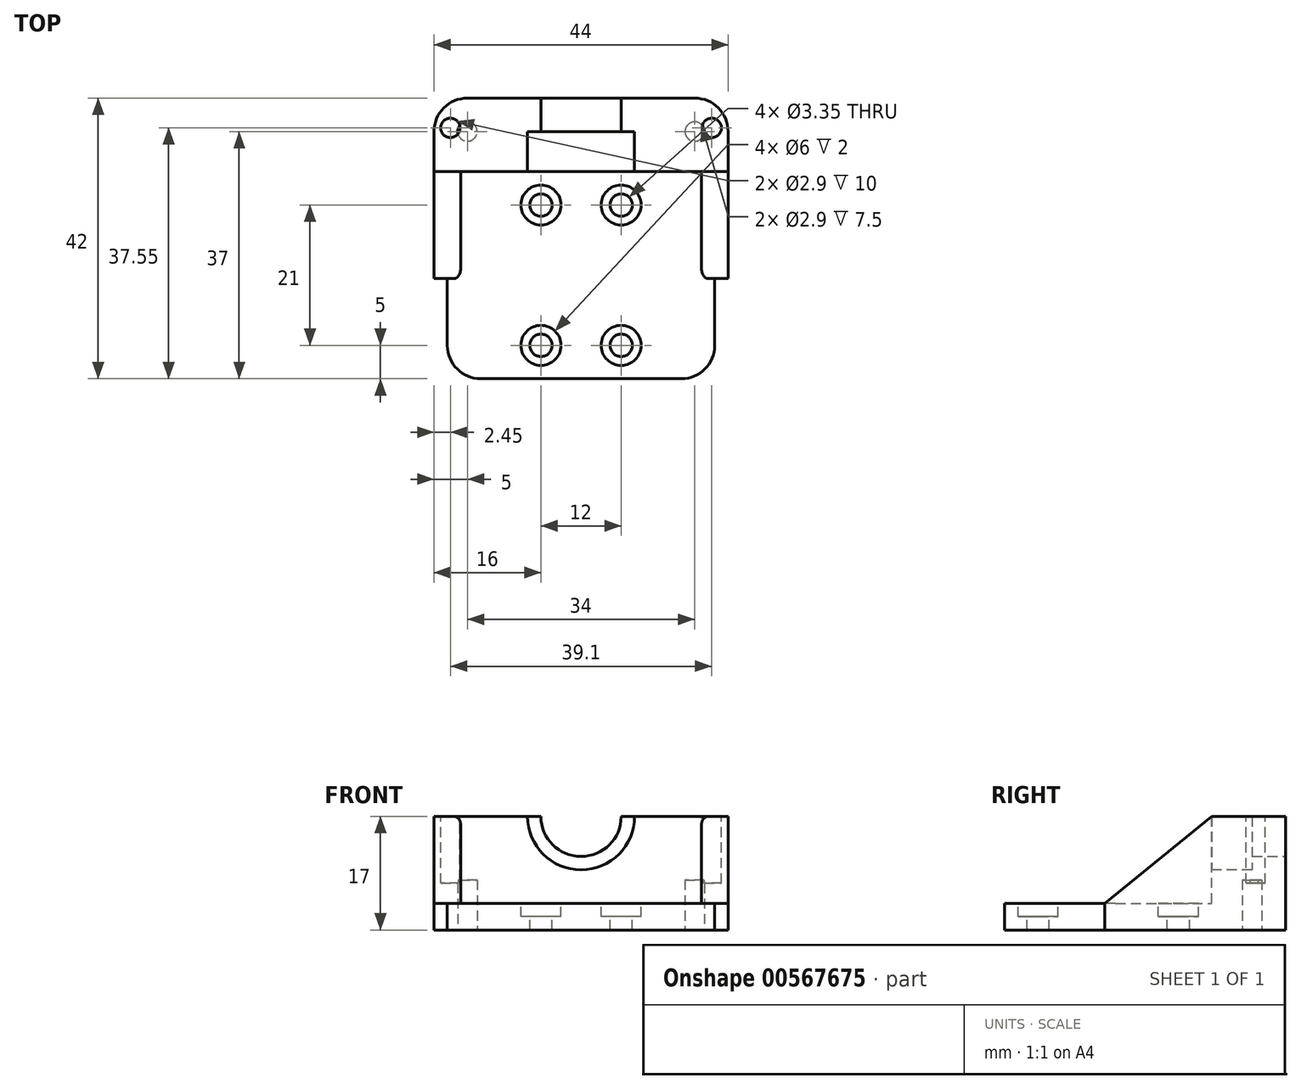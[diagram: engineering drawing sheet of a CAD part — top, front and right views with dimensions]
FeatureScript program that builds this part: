
annotation { "Feature Type Name" : "Feature", "Feature Type Description" : "" }
export const myFeature = defineFeature(function(context is Context, id is Id, definition is map)
    precondition{}
    {
        {
            var Q0;
            Q0=qCreatedBy(makeId("Top.planeOp"),FACE);
            var sketch = newSketch(context, id + "F0", { "sketchPlane" : qUnion([Q0])});
            skLineSegment(sketch, "E0.bottom", {"start": v(0, 0) * mm, "end": v(40, 0) * mm});
            skLineSegment(sketch, "E0.top", {"start": v(0, 42) * mm, "end": v(40, 42) * mm});
            skLineSegment(sketch, "E0.left", {"start": v(0, 0) * mm, "end": v(0, 42) * mm});
            skLineSegment(sketch, "E0.right", {"start": v(40, 0) * mm, "end": v(40, 42) * mm});
            skSolve(sketch);
        }
        {
            var Q0;
            Q0=qSketchRegion(id+"F0",true);
            extrude(context, id + "F1", {"entities" : qUnion([Q0]), "depth" : 4 * mm});
        }
        {
            var Q0;
            Q0=makeQuery(id+"F1.opExtrude","CAP_FACE",FACE,{"disambiguationData":[OSD([sQuery(id+"F0.wireOp",EDGE,"E0.bottom"),sQuery(id+"F0.wireOp",EDGE,"E0.top"),sQuery(id+"F0.wireOp",EDGE,"E0.left"),sQuery(id+"F0.wireOp",EDGE,"E0.right")])],"isStart":false});
            var sketch = newSketch(context, id + "F2", { "sketchPlane" : qUnion([Q0])});
            skCircle(sketch, "E1", {"center": v(14, 26) * mm, "radius": 1.68 * mm});
            skCircle(sketch, "E2", {"center": v(26, 26) * mm, "radius": 1.68 * mm});
            skCircle(sketch, "E3", {"center": v(14, 5) * mm, "radius": 1.68 * mm});
            skCircle(sketch, "E4", {"center": v(26, 5) * mm, "radius": 1.68 * mm});
            skLineSegment(sketch, "E5", {"start": v(14, 26) * mm, "end": v(0, 26) * mm});
            skLineSegment(sketch, "E6", {"start": v(26, 5) * mm, "end": v(40, 5) * mm});
            skCircle(sketch, "E7", {"center": v(14, 26) * mm, "radius": 3 * mm});
            skCircle(sketch, "E8", {"center": v(26, 26) * mm, "radius": 3 * mm});
            skCircle(sketch, "E9", {"center": v(14, 5) * mm, "radius": 3 * mm});
            skCircle(sketch, "E10", {"center": v(26, 5) * mm, "radius": 3 * mm});
            skSolve(sketch);
        }
        {
            var Q0;
            Q0=makeQuery(id+"F2.imprint","IMPRINT",FACE,{"disambiguationData":[TD([[makeQuery(id+"F2.imprint","IMPRINT",EDGE,{"derivedFrom":sQuery(id+"F2.wireOp",EDGE,"E1")}),1.0]])]});
            var Q1;
            Q1=makeQuery(id+"F2.imprint","IMPRINT",FACE,{"disambiguationData":[TD([[makeQuery(id+"F2.imprint","IMPRINT",EDGE,{"derivedFrom":sQuery(id+"F2.wireOp",EDGE,"E2")}),1.0]])]});
            var Q2;
            Q2=makeQuery(id+"F2.imprint","IMPRINT",FACE,{"disambiguationData":[TD([[makeQuery(id+"F2.imprint","IMPRINT",EDGE,{"derivedFrom":sQuery(id+"F2.wireOp",EDGE,"E4")}),1.0]])]});
            var Q3;
            Q3=makeQuery(id+"F2.imprint","IMPRINT",FACE,{"disambiguationData":[TD([[makeQuery(id+"F2.imprint","IMPRINT",EDGE,{"derivedFrom":sQuery(id+"F2.wireOp",EDGE,"E3")}),1.0]])]});
            extrude(context, id + "F3", {"entities" : qUnion([Q0, Q1, Q2, Q3]), "operationType" : NewBodyOperationType.REMOVE, "oppositeDirection" : true, "depth" : 25 * mm});
        }
        {
            var Q0;
            Q0=makeQuery(id+"F1.opExtrude","CAP_FACE",FACE,{"disambiguationData":[OSD([sQuery(id+"F0.wireOp",EDGE,"E0.bottom"),sQuery(id+"F0.wireOp",EDGE,"E0.top"),sQuery(id+"F0.wireOp",EDGE,"E0.left"),sQuery(id+"F0.wireOp",EDGE,"E0.right")])],"isStart":false});
            var sketch = newSketch(context, id + "F4", { "sketchPlane" : qUnion([Q0])});
            skLineSegment(sketch, "E11.bottom", {"start": v(0, 42) * mm, "end": v(40, 42) * mm});
            skLineSegment(sketch, "E11.top", {"start": v(0, 31) * mm, "end": v(40, 31) * mm});
            skLineSegment(sketch, "E11.left", {"start": v(0, 42) * mm, "end": v(0, 31) * mm});
            skLineSegment(sketch, "E11.right", {"start": v(40, 42) * mm, "end": v(40, 31) * mm});
            skSolve(sketch);
        }
        {
            var Q0;
            Q0=qSketchRegion(id+"F4",true);
            extrude(context, id + "F5", {"entities" : qUnion([Q0]), "operationType" : NewBodyOperationType.ADD, "depth" : 13 * mm, "offsetDistance" : 25 * mm});
        }
        {
            var Q0;
            Q0=makeQuery(id+"F5.boolean.opBoolean","MERGE",FACE,{"derivedFrom":[makeQuery(id+"F1.opExtrude","SWEPT_FACE",FACE,{"disambiguationData":[OSD([sQuery(id+"F0.wireOp",EDGE,"E0.top")])]}),makeQuery(id+"F5.opExtrude","SWEPT_FACE",FACE,{"disambiguationData":[OSD([sQuery(id+"F4.wireOp",EDGE,"E11.bottom")])]})]});
            var sketch = newSketch(context, id + "F6", { "sketchPlane" : qUnion([Q0])});
            skCircle(sketch, "E12", {"center": v(-20, 17) * mm, "radius": 6 * mm});
            skSolve(sketch);
        }
        {
            var Q0;
            {var subQ0=makeQuery(id+"F5.opExtrude","CAP_EDGE",EDGE,{"disambiguationData":[OSD([sQuery(id+"F4.wireOp",EDGE,"E11.bottom")])],"isStart":false});var subQ1=sQuery(id+"F6.wireOp",EDGE,"E12");var subQ3=makeQuery(id+"F6.imprint","INTERSECT",VERTEX,{"disambiguationData":[OD(0.0)],"derivedFrom":[subQ0,subQ1]});Q0=makeQuery(id+"F6.imprint","IMPRINT",FACE,{"disambiguationData":[TD([[makeQuery(id+"F6.imprint","IMPRINT",EDGE,{"disambiguationData":[TD([[subQ3,1.0]])],"derivedFrom":subQ1}),1.0]])]});}
            extrude(context, id + "F7", {"entities" : qUnion([Q0]), "operationType" : NewBodyOperationType.REMOVE, "oppositeDirection" : true, "depth" : 6 * mm});
        }
        {
            var Q0;
            Q0=makeQuery(id+"F5.opExtrude","SWEPT_FACE",FACE,{"disambiguationData":[OSD([sQuery(id+"F4.wireOp",EDGE,"E11.top")])]});
            var sketch = newSketch(context, id + "F8", { "sketchPlane" : qUnion([Q0])});
            skCircle(sketch, "E13", {"center": v(20, 17) * mm, "radius": 8 * mm});
            skSolve(sketch);
        }
        {
            var Q0;
            Q0=qSketchRegion(id+"F8",true);
            extrude(context, id + "F9", {"entities" : qUnion([Q0]), "operationType" : NewBodyOperationType.REMOVE, "oppositeDirection" : true, "depth" : 6 * mm});
        }
        {
            var Q0;
            Q0=makeQuery(id+"F2.imprint","IMPRINT",FACE,{"disambiguationData":[TD([[makeQuery(id+"F2.imprint","IMPRINT",EDGE,{"derivedFrom":sQuery(id+"F2.wireOp",EDGE,"E1")}),-1.0]])]});
            var Q1;
            Q1=makeQuery(id+"F2.imprint","IMPRINT",FACE,{"disambiguationData":[TD([[makeQuery(id+"F2.imprint","IMPRINT",EDGE,{"derivedFrom":sQuery(id+"F2.wireOp",EDGE,"E2")}),-1.0]])]});
            var Q2;
            Q2=makeQuery(id+"F2.imprint","IMPRINT",FACE,{"disambiguationData":[TD([[makeQuery(id+"F2.imprint","IMPRINT",EDGE,{"derivedFrom":sQuery(id+"F2.wireOp",EDGE,"E4")}),-1.0]])]});
            var Q3;
            Q3=makeQuery(id+"F2.imprint","IMPRINT",FACE,{"disambiguationData":[TD([[makeQuery(id+"F2.imprint","IMPRINT",EDGE,{"derivedFrom":sQuery(id+"F2.wireOp",EDGE,"E3")}),-1.0]])]});
            extrude(context, id + "F10", {"entities" : qUnion([Q0, Q1, Q2, Q3]), "operationType" : NewBodyOperationType.REMOVE, "oppositeDirection" : true, "depth" : 2 * mm});
        }
        {
            var Q0;
            Q0=makeQuery(id+"F5.boolean.opBoolean","MERGE",FACE,{"derivedFrom":[makeQuery(id+"F1.opExtrude","SWEPT_FACE",FACE,{"disambiguationData":[OSD([sQuery(id+"F0.wireOp",EDGE,"E0.left")])]}),makeQuery(id+"F5.opExtrude","SWEPT_FACE",FACE,{"disambiguationData":[OSD([sQuery(id+"F4.wireOp",EDGE,"E11.left")])]})]});
            var sketch = newSketch(context, id + "F11", { "sketchPlane" : qUnion([Q0])});
            skLineSegment(sketch, "E14.bottom", {"start": v(-42, 0) * mm, "end": v(-31, 0) * mm});
            skLineSegment(sketch, "E14.top", {"start": v(-42, 17) * mm, "end": v(-31, 17) * mm});
            skLineSegment(sketch, "E14.left", {"start": v(-42, 0) * mm, "end": v(-42, 17) * mm});
            skLineSegment(sketch, "E14.right", {"start": v(-31, 0) * mm, "end": v(-31, 17) * mm});
            skSolve(sketch);
        }
        {
            var Q0;
            Q0=qSketchRegion(id+"F11",true);
            extrude(context, id + "F12", {"entities" : qUnion([Q0]), "operationType" : NewBodyOperationType.ADD, "depth" : 2 * mm});
        }
        {
            var Q0;
            Q0=makeQuery(id+"F1.opExtrude","SWEPT_EDGE",EDGE,{"disambiguationData":[OSD([sQuery(id+"F0.wireOp",EDGE,"E0.bottom"),sQuery(id+"F0.wireOp",EDGE,"E0.left")])]});
            var Q1;
            Q1=makeQuery(id+"F1.opExtrude","SWEPT_EDGE",EDGE,{"disambiguationData":[OSD([sQuery(id+"F0.wireOp",EDGE,"E0.bottom"),sQuery(id+"F0.wireOp",EDGE,"E0.right")])]});
            var Q2;
            Q2=makeQuery(id+"F17.opExtrude","TWEAK_EDGE",EDGE,{"derivedFrom":[makeQuery(id+"F1.opExtrude","SWEPT_EDGE",EDGE,{"disambiguationData":[OSD([sQuery(id+"F0.wireOp",EDGE,"E0.bottom"),sQuery(id+"F0.wireOp",EDGE,"E0.left")])]}),makeQuery(id+"F12.opExtrude","CAP_FACE",FACE,{"disambiguationData":[OSD([sQuery(id+"F11.wireOp",EDGE,"E14.bottom"),sQuery(id+"F11.wireOp",EDGE,"E14.top"),sQuery(id+"F11.wireOp",EDGE,"E14.left"),sQuery(id+"F11.wireOp",EDGE,"E14.right")])],"isStart":false})]});
            fillet(context, id + "F13", {"entities" : qUnion([Q0, Q1, Q2]), "radius" : 5 * mm, "tangentPropagation" : true, "allowEdgeOverflow" : false});
        }
        {
            var Q0;
            Q0=makeQuery(id+"F5.boolean.opBoolean","MERGE",FACE,{"derivedFrom":[makeQuery(id+"F1.opExtrude","SWEPT_FACE",FACE,{"disambiguationData":[OSD([sQuery(id+"F0.wireOp",EDGE,"E0.right")])]}),makeQuery(id+"F5.opExtrude","SWEPT_FACE",FACE,{"disambiguationData":[OSD([sQuery(id+"F4.wireOp",EDGE,"E11.right")])]})]});
            var sketch = newSketch(context, id + "F14", { "sketchPlane" : qUnion([Q0])});
            skLineSegment(sketch, "E15.bottom", {"start": v(42, 0) * mm, "end": v(31, 0) * mm});
            skLineSegment(sketch, "E15.top", {"start": v(42, 17) * mm, "end": v(31, 17) * mm});
            skLineSegment(sketch, "E15.left", {"start": v(42, 0) * mm, "end": v(42, 17) * mm});
            skLineSegment(sketch, "E15.right", {"start": v(31, 0) * mm, "end": v(31, 17) * mm});
            skSolve(sketch);
        }
        {
            var Q0;
            Q0=qSketchRegion(id+"F14",true);
            extrude(context, id + "F15", {"entities" : qUnion([Q0]), "operationType" : NewBodyOperationType.ADD, "depth" : 2 * mm});
        }
        {
            var Q0;
            Q0=qSketchRegion(id+"F14",true);
            extrude(context, id + "F16", {"entities" : qUnion([Q0]), "operationType" : NewBodyOperationType.ADD, "depth" : 2 * mm});
        }
        {
            var Q0;
            Q0=makeQuery(id+"F5.boolean.opBoolean","MERGE",FACE,{"derivedFrom":[makeQuery(id+"F1.opExtrude","SWEPT_FACE",FACE,{"disambiguationData":[OSD([sQuery(id+"F0.wireOp",EDGE,"E0.left")])]}),makeQuery(id+"F5.opExtrude","SWEPT_FACE",FACE,{"disambiguationData":[OSD([sQuery(id+"F4.wireOp",EDGE,"E11.left")])]})]});
            var Q1;
            Q1=makeQuery(id+"F12.opExtrude","CAP_FACE",FACE,{"disambiguationData":[OSD([sQuery(id+"F11.wireOp",EDGE,"E14.bottom"),sQuery(id+"F11.wireOp",EDGE,"E14.top"),sQuery(id+"F11.wireOp",EDGE,"E14.left"),sQuery(id+"F11.wireOp",EDGE,"E14.right")])],"isStart":false});
            extrude(context, id + "F17", {"entities" : qUnion([Q0]), "operationType" : NewBodyOperationType.ADD, "endBound" : BoundingType.UP_TO_SURFACE, "depth" : 25 * mm, "endBoundEntityFace" : qUnion([Q1]), "offsetDistance" : 25 * mm});
        }
        {
            var Q0;
            Q0=makeQuery(id+"F5.boolean.opBoolean","MERGE",FACE,{"derivedFrom":[makeQuery(id+"F1.opExtrude","SWEPT_FACE",FACE,{"disambiguationData":[OSD([sQuery(id+"F0.wireOp",EDGE,"E0.right")])]}),makeQuery(id+"F5.opExtrude","SWEPT_FACE",FACE,{"disambiguationData":[OSD([sQuery(id+"F4.wireOp",EDGE,"E11.right")])]})]});
            var Q1;
            Q1=makeQuery(id+"F15.opExtrude","CAP_FACE",FACE,{"disambiguationData":[OSD([sQuery(id+"F14.wireOp",EDGE,"E15.bottom"),sQuery(id+"F14.wireOp",EDGE,"E15.top"),sQuery(id+"F14.wireOp",EDGE,"E15.left"),sQuery(id+"F14.wireOp",EDGE,"E15.right")])],"isStart":false});
            extrude(context, id + "F18", {"entities" : qUnion([Q0]), "operationType" : NewBodyOperationType.ADD, "endBound" : BoundingType.UP_TO_SURFACE, "depth" : 25 * mm, "endBoundEntityFace" : qUnion([Q1]), "offsetDistance" : 25 * mm});
        }
        {
            var Q0;
            {var subQ0=sQuery(id+"F4.wireOp",EDGE,"E11.bottom");var subQ1=sQuery(id+"F4.wireOp",EDGE,"E11.top");var subQ2=sQuery(id+"F4.wireOp",EDGE,"E11.left");Q0=makeQuery(id+"F9.boolean.opBoolean","SPLIT",FACE,{"disambiguationData":[TD([makeQuery(id+"F1.opExtrude","SWEPT_FACE",FACE,{"disambiguationData":[OSD([sQuery(id+"F0.wireOp",EDGE,"E0.left")])]})])],"derivedFrom":makeQuery(id+"F5.opExtrude","CAP_FACE",FACE,{"disambiguationData":[OSD([subQ0,subQ1,subQ2,sQuery(id+"F4.wireOp",EDGE,"E11.right")])],"isStart":false})});}
            var sketch = newSketch(context, id + "F19", { "sketchPlane" : qUnion([Q0])});
            skCircle(sketch, "E16", {"center": v(0.45, 37.55) * mm, "radius": 1.45 * mm});
            skCircle(sketch, "E17", {"center": v(39.55, 37.55) * mm, "radius": 1.45 * mm});
            skSolve(sketch);
        }
        {
            var Q0;
            Q0=qSketchRegion(id+"F19",true);
            extrude(context, id + "F20", {"entities" : qUnion([Q0]), "operationType" : NewBodyOperationType.REMOVE, "oppositeDirection" : true, "depth" : 10 * mm, "offsetDistance" : 25 * mm});
        }
        {
            var Q0;
            Q0=makeQuery(id+"F12.opExtrude","CAP_EDGE",EDGE,{"disambiguationData":[OSD([sQuery(id+"F11.wireOp",EDGE,"E14.left")])],"isStart":false});
            var Q1;
            Q1=makeQuery(id+"F15.opExtrude","CAP_EDGE",EDGE,{"disambiguationData":[OSD([sQuery(id+"F14.wireOp",EDGE,"E15.left")])],"isStart":false});
            fillet(context, id + "F21", {"entities" : qUnion([Q0, Q1]), "radius" : 5 * mm, "tangentPropagation" : true, "allowEdgeOverflow" : false});
        }
        {
            var Q0;
            Q0=makeQuery(id+"F2.imprint","IMPRINT",FACE,{"disambiguationData":[TD([[makeQuery(id+"F2.imprint","IMPRINT",EDGE,{"derivedFrom":sQuery(id+"F2.wireOp",EDGE,"E1")}),-1.0]])]});
            var Q1;
            Q1=makeQuery(id+"F2.imprint","IMPRINT",FACE,{"disambiguationData":[TD([[makeQuery(id+"F2.imprint","IMPRINT",EDGE,{"derivedFrom":sQuery(id+"F2.wireOp",EDGE,"E2")}),-1.0]])]});
            var Q2;
            Q2=makeQuery(id+"F2.imprint","IMPRINT",FACE,{"disambiguationData":[TD([[makeQuery(id+"F2.imprint","IMPRINT",EDGE,{"derivedFrom":sQuery(id+"F2.wireOp",EDGE,"E1")}),1.0]])]});
            var Q3;
            Q3=makeQuery(id+"F2.imprint","IMPRINT",FACE,{"disambiguationData":[TD([[makeQuery(id+"F2.imprint","IMPRINT",EDGE,{"derivedFrom":sQuery(id+"F2.wireOp",EDGE,"E2")}),1.0]])]});
            extrude(context, id + "F22", {"entities" : qUnion([Q0, Q1, Q2, Q3]), "operationType" : NewBodyOperationType.REMOVE, "depth" : 25 * mm});
        }
        {
            var Q0;
            Q0=makeQuery(id+"F15.boolean.opBoolean","MERGE",FACE,{"derivedFrom":[makeQuery(id+"F12.boolean.opBoolean","MERGE",FACE,{"derivedFrom":[makeQuery(id+"F1.opExtrude","CAP_FACE",FACE,{"disambiguationData":[OSD([sQuery(id+"F0.wireOp",EDGE,"E0.bottom"),sQuery(id+"F0.wireOp",EDGE,"E0.top"),sQuery(id+"F0.wireOp",EDGE,"E0.left"),sQuery(id+"F0.wireOp",EDGE,"E0.right")])],"isStart":true}),makeQuery(id+"F12.opExtrude","SWEPT_FACE",FACE,{"disambiguationData":[OSD([sQuery(id+"F11.wireOp",EDGE,"E14.bottom")])]})]}),makeQuery(id+"F15.opExtrude","SWEPT_FACE",FACE,{"disambiguationData":[OSD([sQuery(id+"F14.wireOp",EDGE,"E15.bottom")])]})]});
            var sketch = newSketch(context, id + "F23", { "sketchPlane" : qUnion([Q0])});
            skCircle(sketch, "E18", {"center": v(37, -37) * mm, "radius": 1.45 * mm});
            skCircle(sketch, "E19", {"center": v(3, -37) * mm, "radius": 1.45 * mm});
            skSolve(sketch);
        }
        {
            var Q0;
            Q0=qSketchRegion(id+"F23",true);
            extrude(context, id + "F24", {"entities" : qUnion([Q0]), "operationType" : NewBodyOperationType.REMOVE, "oppositeDirection" : true, "depth" : 7.5 * mm, "offsetDistance" : 25 * mm});
        }
        {
            var Q0;
            Q0=makeQuery(id+"F17.opExtrude","SWEPT_FACE",FACE,{"disambiguationData":[OSD([sQuery(id+"F0.wireOp",EDGE,"E0.bottom"),sQuery(id+"F0.wireOp",EDGE,"E0.left"),sQuery(id+"F4.wireOp",EDGE,"E11.left")])]});
            var Q1;
            Q1=makeQuery(id+"F18.opExtrude","SWEPT_FACE",FACE,{"disambiguationData":[OSD([sQuery(id+"F0.wireOp",EDGE,"E0.bottom"),sQuery(id+"F0.wireOp",EDGE,"E0.right"),sQuery(id+"F4.wireOp",EDGE,"E11.right")])]});
            extrude(context, id + "F25", {"entities" : qUnion([Q0, Q1]), "operationType" : NewBodyOperationType.REMOVE, "oppositeDirection" : true, "depth" : 10 * mm, "offsetDistance" : 25 * mm});
        }
        {
            var Q0;
            {var subQ0=sQuery(id+"F11.wireOp",EDGE,"E14.right");var subQ1=sQuery(id+"F11.wireOp",EDGE,"E14.left");var subQ2=sQuery(id+"F11.wireOp",EDGE,"E14.top");var subQ3=sQuery(id+"F11.wireOp",EDGE,"E14.bottom");Q0=makeQuery(id+"F17.boolean.opBoolean","MERGE",FACE,{"derivedFrom":[makeQuery(id+"F12.opExtrude","CAP_FACE",FACE,{"disambiguationData":[OSD([subQ3,subQ2,subQ1,subQ0])],"isStart":false}),makeQuery(id+"F17.opExtrude","CAP_FACE",FACE,{"disambiguationData":[OSD([subQ3,subQ2,subQ1,subQ0])],"isStart":false})]});}
            var sketch = newSketch(context, id + "F26", { "sketchPlane" : qUnion([Q0])});
            skLineSegment(sketch, "E20", {"start": v(-31, 17) * mm, "end": v(-15, 4) * mm});
            skLineSegment(sketch, "E21", {"start": v(-15, 4) * mm, "end": v(-31, 4) * mm});
            skLineSegment(sketch, "E22", {"start": v(-31, 4) * mm, "end": v(-31, 17) * mm});
            skSolve(sketch);
        }
        {
            var Q0;
            Q0=makeQuery(id+"F26.imprint","IMPRINT",FACE,{"disambiguationData":[TD([[makeQuery(id+"F26.imprint","IMPRINT",EDGE,{"derivedFrom":sQuery(id+"F26.wireOp",EDGE,"E20")}),-1.0]])]});
            extrude(context, id + "F27", {"entities" : qUnion([Q0]), "operationType" : NewBodyOperationType.ADD, "oppositeDirection" : true, "depth" : 4 * mm, "offsetDistance" : 25 * mm});
        }
        {
            var Q0;
            {var subQ0=sQuery(id+"F14.wireOp",EDGE,"E15.right");var subQ1=sQuery(id+"F14.wireOp",EDGE,"E15.left");var subQ2=sQuery(id+"F14.wireOp",EDGE,"E15.top");var subQ3=sQuery(id+"F14.wireOp",EDGE,"E15.bottom");Q0=makeQuery(id+"F18.boolean.opBoolean","MERGE",FACE,{"derivedFrom":[makeQuery(id+"F15.opExtrude","CAP_FACE",FACE,{"disambiguationData":[OSD([subQ3,subQ2,subQ1,subQ0])],"isStart":false}),makeQuery(id+"F18.opExtrude","CAP_FACE",FACE,{"disambiguationData":[OSD([subQ3,subQ2,subQ1,subQ0])],"isStart":false})]});}
            var sketch = newSketch(context, id + "F28", { "sketchPlane" : qUnion([Q0])});
            skLineSegment(sketch, "E23", {"start": v(31, 17) * mm, "end": v(15, 4) * mm});
            skLineSegment(sketch, "E24", {"start": v(15, 4) * mm, "end": v(31, 4) * mm});
            skLineSegment(sketch, "E25", {"start": v(31, 4) * mm, "end": v(31, 17) * mm});
            skSolve(sketch);
        }
        {
            var Q0;
            Q0=makeQuery(id+"F28.imprint","IMPRINT",FACE,{"disambiguationData":[TD([[makeQuery(id+"F28.imprint","IMPRINT",EDGE,{"derivedFrom":sQuery(id+"F28.wireOp",EDGE,"E23")}),1.0]])]});
            extrude(context, id + "F29", {"entities" : qUnion([Q0]), "operationType" : NewBodyOperationType.ADD, "oppositeDirection" : true, "depth" : 4 * mm, "offsetDistance" : 25 * mm});
        }
        {
            var Q0;
            Q0=makeQuery(id+"F27.opExtrude","CAP_EDGE",EDGE,{"disambiguationData":[OSD([sQuery(id+"F26.wireOp",EDGE,"E21")])],"isStart":false});
            var Q1;
            Q1=makeQuery(id+"F27.opExtrude","CAP_EDGE",EDGE,{"disambiguationData":[OSD([sQuery(id+"F26.wireOp",EDGE,"E20")])],"isStart":false});
            var Q2;
            Q2=makeQuery(id+"F29.opExtrude","CAP_EDGE",EDGE,{"disambiguationData":[OSD([sQuery(id+"F28.wireOp",EDGE,"E24")])],"isStart":false});
            var Q3;
            Q3=makeQuery(id+"F29.opExtrude","CAP_EDGE",EDGE,{"disambiguationData":[OSD([sQuery(id+"F28.wireOp",EDGE,"E23")])],"isStart":false});
            fillet(context, id + "F30", {"entities" : qUnion([Q0, Q1, Q2, Q3]), "radius" : 1 * mm, "allowEdgeOverflow" : false});
        }
    });
